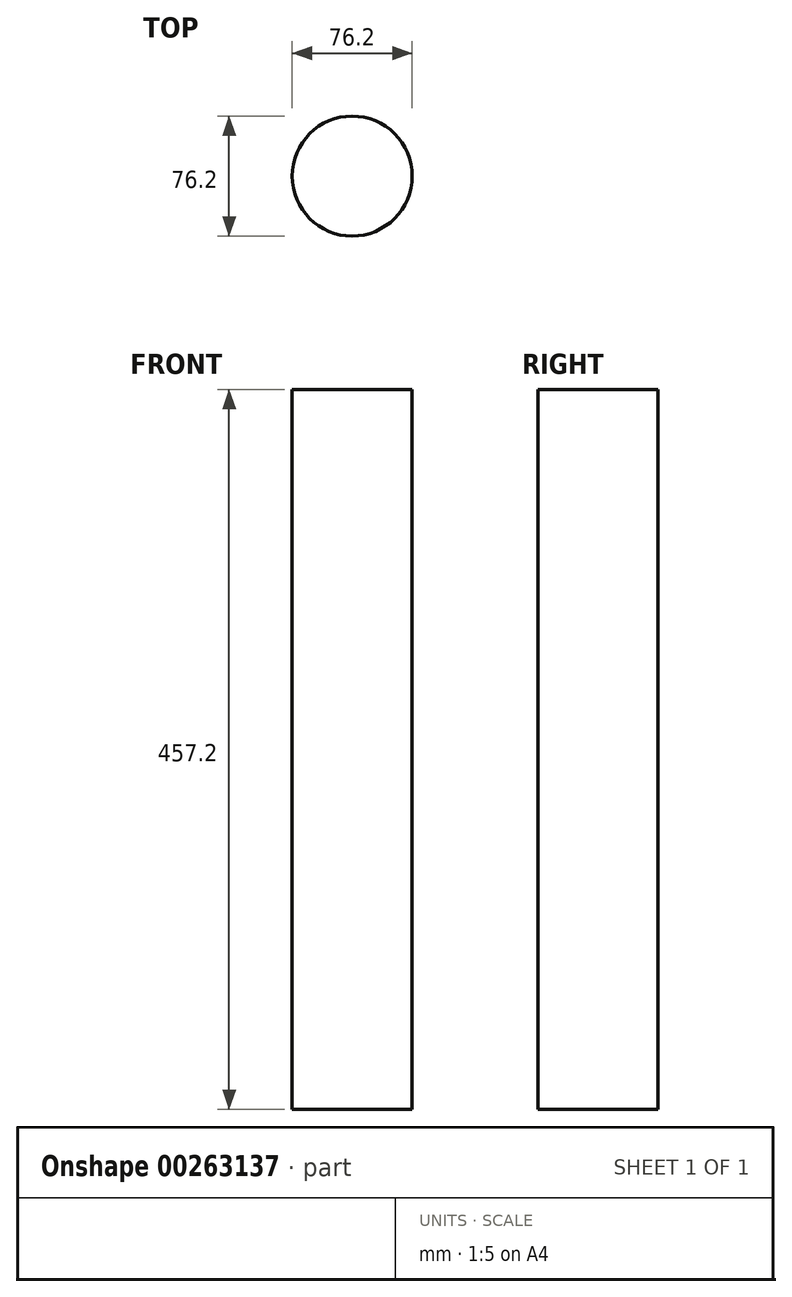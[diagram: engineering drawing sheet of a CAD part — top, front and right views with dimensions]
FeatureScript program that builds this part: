
annotation { "Feature Type Name" : "Feature", "Feature Type Description" : "" }
export const myFeature = defineFeature(function(context is Context, id is Id, definition is map)
    precondition{}
    {
        {
            var Q0;
            Q0=qCreatedBy(makeId("Front.planeOp"),FACE);
            var sketch = newSketch(context, id + "F0", { "sketchPlane" : qUnion([Q0])});
            skLineSegment(sketch, "E0", {"start": v(0, 0) * mm, "end": v(0, 93.37) * mm});
            skLineSegment(sketch, "E1", {"start": v(0, 46.69) * mm, "end": v(120.98, -116.57) * mm});
            skLineSegment(sketch, "E2", {"start": v(120.98, -116.57) * mm, "end": v(120.98, -319.77) * mm});
            skSolve(sketch);
        }
        {
            var Q0;
            Q0=qCreatedBy(makeId("Top.planeOp"),FACE);
            var sketch = newSketch(context, id + "F1", { "sketchPlane" : qUnion([Q0])});
            skCircle(sketch, "E3", {"center": v(0, 0) * mm, "radius": 38.1 * mm});
            skSolve(sketch);
        }
        {
            var Q0;
            Q0=makeQuery(id+"F1.imprint","IMPRINT",FACE,{"disambiguationData":[TD([[makeQuery(id+"F1.imprint","IMPRINT",EDGE,{"derivedFrom":sQuery(id+"F1.wireOp",EDGE,"E3")}),1.0]])]});
            var Q1;
            Q1=sQuery(id+"F1.wireOp",EDGE,"E3");
            extrude(context, id + "F2", {"entities" : qUnion([Q0]), "bodyType" : ToolBodyType.SURFACE, "surfaceEntities" : qUnion([Q1]), "endBound" : BoundingType.SYMMETRIC, "depth" : 457.2 * mm});
        }
        {
            var Q0;
            Q0=qCreatedBy(makeId("Top.planeOp"),FACE);
            var Q1;
            Q1=sQuery(id+"F0.wireOp",VERTEX,"E2.end");
            cPlane(context, id + "F3", {"entities" : qUnion([Q0, Q1]), "cplaneType" : CPlaneType.PLANE_POINT, "offset" : 25.4 * mm, "oppositeDirection" : true, "width" : 152.4 * mm, "height" : 152.4 * mm});
        }
        {
            var Q0;
            Q0=qCreatedBy(id+"F3.planeOp",FACE);
            var sketch = newSketch(context, id + "F4", { "sketchPlane" : qUnion([Q0])});
            skCircle(sketch, "E4", {"center": v(120.98, 0) * mm, "radius": 31.75 * mm});
            skSolve(sketch);
        }
    });
